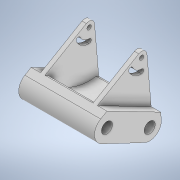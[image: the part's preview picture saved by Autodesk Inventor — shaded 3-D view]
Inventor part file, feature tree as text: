
AUTODESK INVENTOR PART (.ipt)
format: ipt  version: 2020 (Build 240168000, 168)  size: 249,856 bytes
history: native  units: in
note: dims shown in document units (in); Inventor stores cm internally (conversion verified against a paired STEP export)
features: extrude x8, sketch x8, projected_geometry x4, plane x1
ambient origin geometry x8: Origin, YZ Plane, XZ Plane, XY Plane, X Axis, Y Axis, Z Axis, Center Point
bodies: Solid1 (feature_tree)
feature tree (21):
  extrude  "Extrusion1"  Depth=1.378in TaperAngle=0.0deg
  extrude  "Extrusion2"  Depth=0.1969in
  extrude  "Extrusion3"  Depth=0.0787in
  extrude  "Extrusion4"  Depth=1.378in
  plane  "Work Plane1"
  extrude  "Extrusion5"  Depth=0.0787in
  extrude  "Extrusion6"  Depth=0.0787in
  extrude  "Extrusion7"  Depth=1.378in
  extrude  "Extrusion8"  Depth=0.1732in TaperAngle=0.0deg
  sketch  "Sketch1"  dims[d0=0.2008in d1=0.2008in d2=1.378in d3=0.0in]
  sketch  "Sketch2"  dims[d4=0.7874in d5=0.1969in]
  sketch  "Sketch4"  dims[d6=1.378in d7=0.0in d8=0.0787in]
  projected_geometry  "Projected Loop1"
  sketch  "Sketch5"  dims[d9=1.378in d10=0.0in d11=0.4331in]
  projected_geometry  "Projected Loop2"
  sketch  "Sketch6"  dims[d12=0.0787in d13=0.0787in]
  sketch  "Sketch7"  dims[d14=0.0787in d15=0.4466in]
  sketch  "Sketch8"  dims[d16=1.378in d17=0.0in d18=0.437in]
  projected_geometry  "Projected Loop3"
  sketch  "Sketch9"  dims[d19=0.1181in d20=0.8357in d21=0.0in d22=0.315in d23=0.315in d24=1.378in d25=0.0in d26=0.1732in d27=0.0in d28=0.1732in d29=0.0in]
  projected_geometry  "Projected Loop4"
